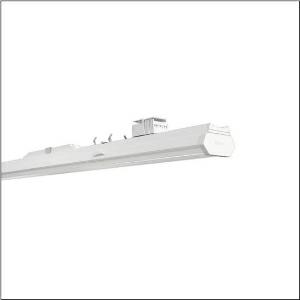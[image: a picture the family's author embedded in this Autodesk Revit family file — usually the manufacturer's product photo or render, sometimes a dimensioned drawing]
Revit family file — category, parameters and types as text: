
# Revit family: licross_r__11_protected_mo_51td1bmn49xg_0ef7
name_source: partatom
category: Lighting Fixtures
units: mm (PartAtom-declared; Revit-internal decimal feet)

## family parameters
Cut with Voids When Loaded = No
Host = Face
Light Source = No
Part Type = Normal
Room Calculation Point = No
Round Connector Dimension = Use Diameter
Shared = No

## types (1)
- --- (1 x LED, 9410 lm, 55.3 W, 4000K)
    Apparent Load = 55 VA
    CIE Flux Codes = 54 82 95 97 100
    Color Rendering = 80
    Color Temperature = 4000K
    Default Elevation = 1800 mm
    Description = Licross® 11 Protected MO, luminaire insert, of sheet steel, galvanised, coil coated, white, length: 1.500mm, width: 90mm, height: 101mm, LED rated luminous flux: 9.420lm, light colour: 840, control gear: ON/OFF Multilumen, with plug, 3-pole, with phase selection, mains connection: 220..240V, AC, 50/60Hz, rated input power: 55W, internal wiring halogen-free, primary optical cover: cover, of PMMA, light emission: direct distribution, primary light characteristic: symmetric, protection rating (complete): IP54, insulation class (complete): insulation class I (protective earthing), certification: CE, ENEC, VDE, UKCA, protection symbol: D if used in an environment with non-conductive dust loads with corresponding accessories, impact resistance: IK06, permissible ambient temperature for indoor applications: -35..+40°C, corresponds to IFS (International Featured Standards) requirements for safety and quality in the food industry, reducing of maximum allowable ambient temperature of 5°C with ceiling mounting, LABS conformity tested according to VDMA 24364:2018-05, packaging unit: 1 piece
    Height = 92 mm
    Lamp = 1 x LED
    Lamp Light Flux = 9410 lm
    Lamp Power = 55.3 W
    Lamp count = 1
    Length = 1500 mm
    Luminous efficacy = 170 lm/W
    Manufacturer = Siteco
    ModVariant = No
    Model = 51TD1BMN49XG
    Mounting Place = Ceiling
    Mounting Type = Pendant
    Number of Poles = 1
    OnlyDefault = Yes
    Power Factor = 1
    Product Name = Licross® 11 Protected MO
    Product group = luminaire insert | ceiling pendant
    ProductGroupID = 902
    Protection Class = Protection class I
    Protection Degree = IP 54
    RLX_Detail_Level = 1
    RLX_Emergency_Light_Flux = 0 lm
    RLX_Emergency_Type = 0
    RLX_Emergency_Type_DB = No
    RlxData = <blob elided: 22141 chars, md5=3aa30b71>
    Socket = socket
    Standby Power = 0 W
    System Light Flux = 9410 lm
    System Power = 55 W
    Type Comments = factory setting: luminous flux: 100 % | (A | C | E) | 126 mA
    Type Image = l_1256145.jpg
    URL = http://relux.com
    VarID = @adj_107539
    Voltage = 0 V
    Weight = 0.00 kg
    Width = 88 mm

## geometry (parser evidence)
native form markers: Blend x4, Sweep x11
no freeform markers — native parametric forms only
